# Revit family: NLRS_32_DO_Medicare_EI1
name_source: partatom
category: Doors
units: mm (PartAtom-declared; Revit-internal decimal feet)

## family parameters
Always vertical = Yes
Cut with Voids When Loaded = Yes
Host = Wall
OmniClass Number = 23.30.10.00
OmniClass Title = Doors
Room Calculation Point = No
Shared = Yes

## types (2) — shared parameters
Analytic Construction = <None>
Assembly Code = 32.32
IFCExportAs = IfcDoorType
IFCExportType = DOOR
MFX_L_Height_Handle = 1255 mm  [stored 4.11745 ft]
MFX_L_Width_Window = 300 mm
MFX_Motor_on_top and manual = Yes
MFX_Opener_Var = 195 mm  [stored 0.639764 ft]
MFX_Opener_Var_2 = 90 mm  [stored 0.295276 ft]
MFX_YN_Canopy_Ceiling = No
MFX_YN_Canopy_Low = No
MFX_YN_Opener_Hermetic_Lever = Yes
MFX_YN_Opener_no_opener = No
Manufacturer = Metaflex
Model = Medinox
Type Comments = Metaflex schuifdeur Medinox
URL = www.metaflex.nl
Wall Closure = By host
zero-valued in all types: MFX_L_Canopy120, MFX_L_Wall_finish opening, Rough Width, Thickness

## per-type parameters (varying)
| type | Comment | Height | MFX_L_Centre_Height_Window | MFX_L_FP | MFX_L_Height_Canopy | MFX_L_Height_Cut-Out (Size Wall Opening) | MFX_L_Height_Window | MFX_L_IFH | MFX_L_IFH_1 | MFX_L_IFH_min max | MFX_L_IFW | MFX_L_IFW_Min_Max | MFX_L_Width_Cut-Out_Size Wall Opening | MFX_YN_Canopy_BBU | MFX_YN_Canopy_High | MFX_YN_Door | MFX_YN_Door_With_Window_300x600 | MFX_YN_Door_With_Window_400x400 | MFX_YN_Door_With_Window_600x600 | MFX_YN_Door_With_Window_852x852 | Rough Height | Width |
| Medicare_EI1 | WHEN A DIFFERENT WINDOW SIZE IS REQUIRED (BE AWARE THAT SPACE AROUND THE WINDOW IS 200MM!)  , PLEASE CHECK WITH METAFLEX | 2268 mm  [stored 7.44094 ft] | 1600 mm  [stored 5.24934 ft] | 1000 mm  [stored 3.28084 ft] | 2324 mm  [stored 7.62467 ft] | 2311 mm  [stored 7.58202 ft] | 300 mm | 2200 mm  [stored 7.21785 ft] | 2200 mm  [stored 7.21785 ft] | 2268 mm  [stored 7.44094 ft] | 1195 mm | 1000 mm  [stored 3.28084 ft] | 1300 mm  [stored 4.26509 ft] | No | Yes | Yes | No | No | No | No | 2243 mm  [stored 7.35892 ft] | 1000 mm  [stored 3.28084 ft] |
| Medicare_Door_300*600 | WHEN A DIFFERENT WINDOW SIZE IS REQUIRED, PLEASE CHECK WITH METAFLEX | 2700 mm  [stored 8.85827 ft] | 600 mm | 1500 mm  [stored 4.92126 ft] | 2756 mm  [stored 9.04199 ft] | 2743 mm | 600 mm | 2700 mm  [stored 8.85827 ft] | 2632 mm  [stored 8.63517 ft] | 2700 mm  [stored 8.85827 ft] | 1695 mm | 1500 mm  [stored 4.92126 ft] | 1800 mm  [stored 5.90551 ft] | Yes | No | No | Yes | Yes | Yes | Yes | 2675 mm | 1500 mm  [stored 4.92126 ft] |

note: [stored X ft] marks values corroborated as IEEE doubles in the binary element streams (Revit-internal decimal feet)

## geometry (parser evidence)
native form markers: Blend x4, Sweep x67
no freeform markers — native parametric forms only
